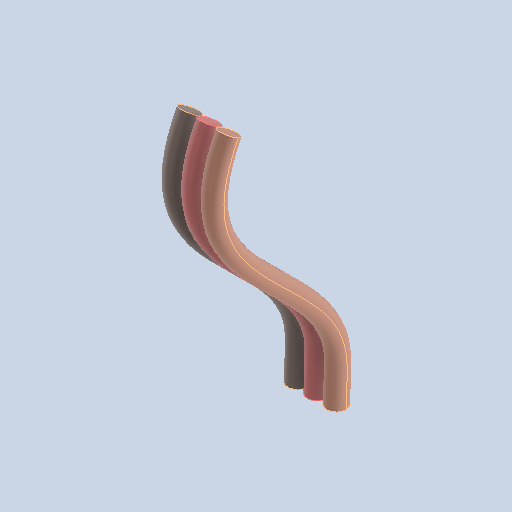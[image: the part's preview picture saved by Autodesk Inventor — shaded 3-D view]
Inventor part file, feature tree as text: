
AUTODESK INVENTOR PART (.ipt)
format: ipt  version: 2025.1 (Build 291241000, 241)  size: 204,288 bytes
history: native  units: mm
features: sweep x3
ambient origin geometry x8: Origin, YZ Plane, XZ Plane, XY Plane, X Axis, Y Axis, Z Axis, Center Point
bodies: Volumenkörper1 (feature_tree), Volumenkörper2 (feature_tree), Volumenkörper3 (feature_tree)
feature tree (3):
  sweep  "Sweep2[1]"
  sweep  "Sweep2[2]"
  sweep  "Sweep2[3]"
